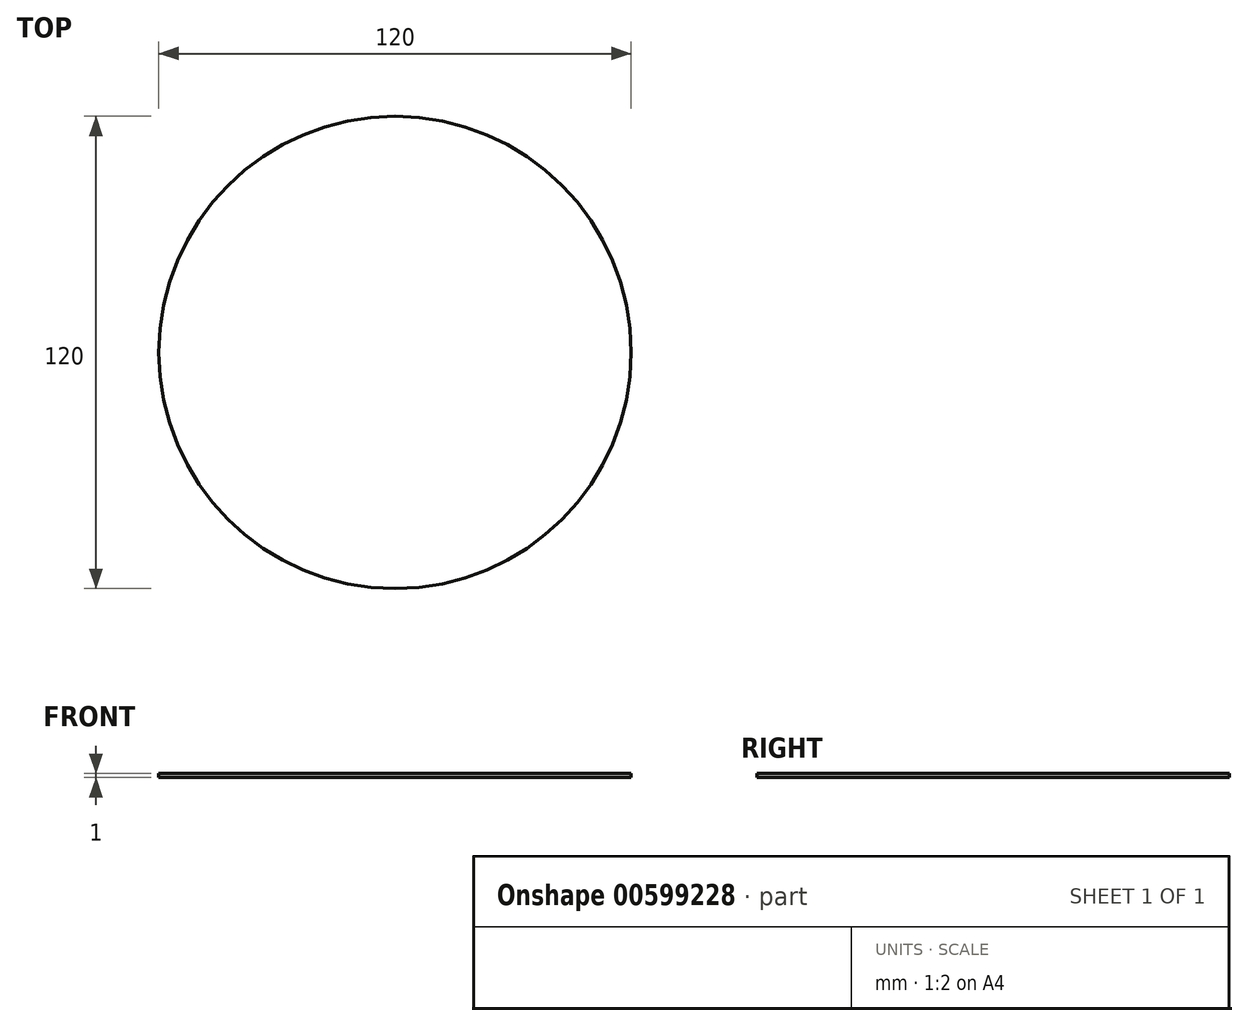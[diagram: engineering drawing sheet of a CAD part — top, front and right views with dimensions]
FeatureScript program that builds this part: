
annotation { "Feature Type Name" : "Feature", "Feature Type Description" : "" }
export const myFeature = defineFeature(function(context is Context, id is Id, definition is map)
    precondition{}
    {
        {
            var Q0;
            Q0=qCreatedBy(makeId("Top.planeOp"),FACE);
            var sketch = newSketch(context, id + "F0", { "sketchPlane" : qUnion([Q0])});
            skCircle(sketch, "E0", {"center": v(0, 0) * mm, "radius": 60 * mm});
            skSolve(sketch);
        }
        {
            var Q0;
            Q0=makeQuery(id+"F0.imprint","IMPRINT",FACE,{"disambiguationData":[TD([[makeQuery(id+"F0.imprint","IMPRINT",EDGE,{"derivedFrom":sQuery(id+"F0.wireOp",EDGE,"E0")}),1.0]])]});
            extrude(context, id + "F1", {"entities" : qUnion([Q0]), "depth" : 1 * mm, "offsetDistance" : 25 * mm});
        }
    });
